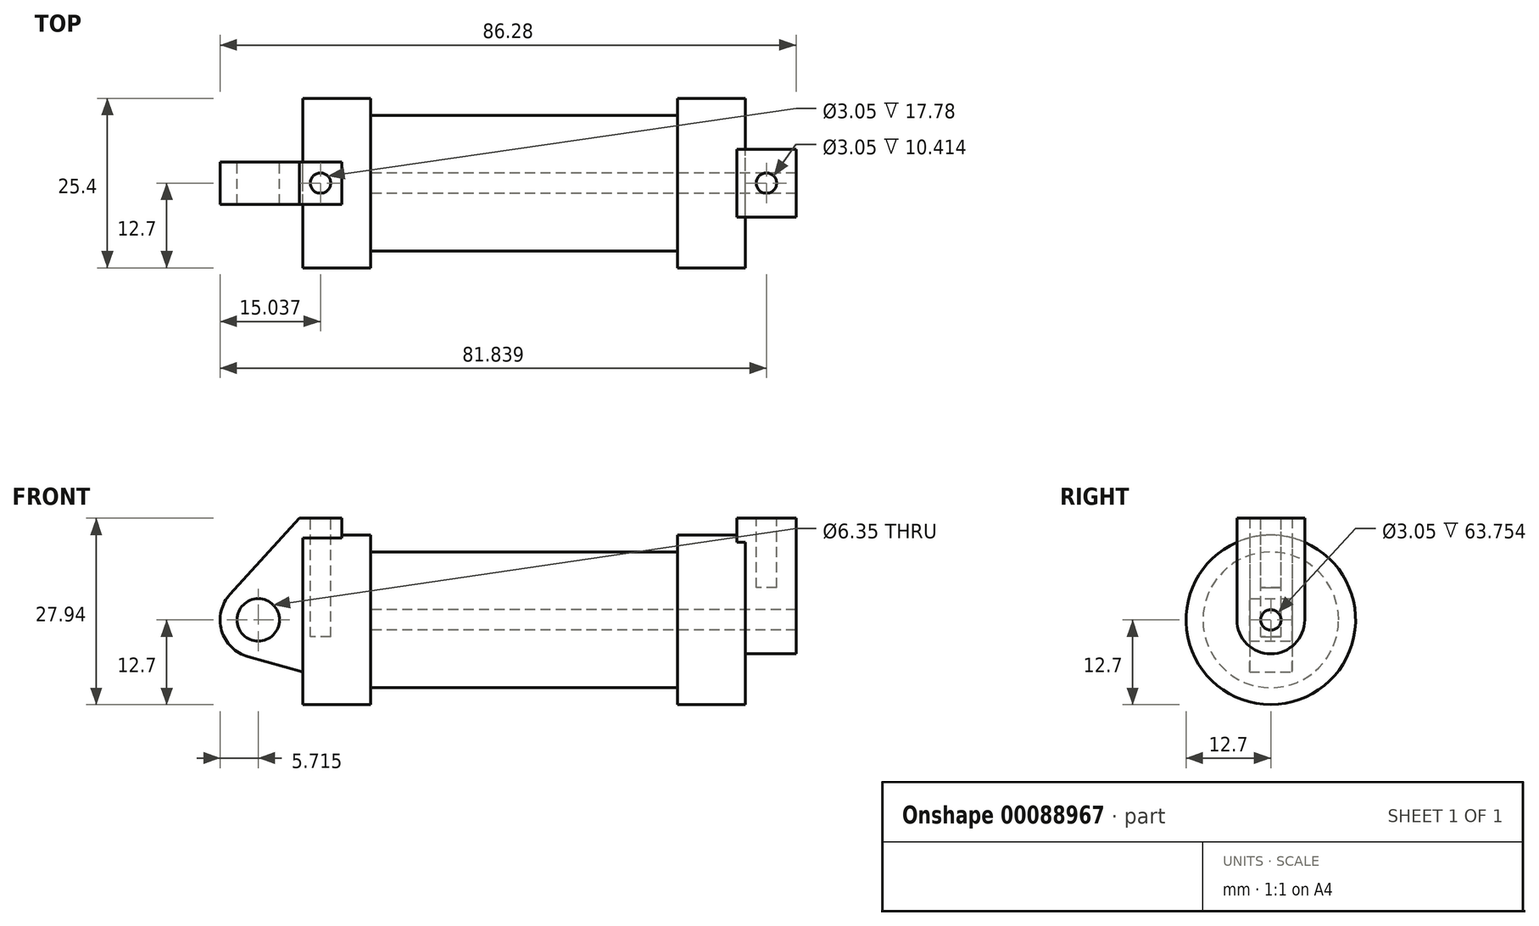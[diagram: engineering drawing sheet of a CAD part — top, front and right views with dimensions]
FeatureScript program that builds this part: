
annotation { "Feature Type Name" : "Feature", "Feature Type Description" : "" }
export const myFeature = defineFeature(function(context is Context, id is Id, definition is map)
    precondition{}
    {
        {
            var Q0;
            Q0=qCreatedBy(makeId("Front.planeOp"),FACE);
            var sketch = newSketch(context, id + "F0", { "sketchPlane" : qUnion([Q0])});
            skLineSegment(sketch, "E0", {"start": v(0, 0) * mm, "end": v(0, 12.7) * mm});
            skLineSegment(sketch, "E1", {"start": v(0, 12.7) * mm, "end": v(10.16, 12.7) * mm});
            skLineSegment(sketch, "E2", {"start": v(10.16, 12.7) * mm, "end": v(10.16, 10.16) * mm});
            skLineSegment(sketch, "E3", {"start": v(10.16, 10.16) * mm, "end": v(56.13, 10.16) * mm});
            skLineSegment(sketch, "E4", {"start": v(56.13, 10.16) * mm, "end": v(56.13, 12.7) * mm});
            skLineSegment(sketch, "E5", {"start": v(56.13, 12.7) * mm, "end": v(66.3, 12.7) * mm});
            skLineSegment(sketch, "E6", {"start": v(66.3, 12.7) * mm, "end": v(66.3, 0) * mm});
            skLineSegment(sketch, "E7", {"start": v(66.3, 0) * mm, "end": v(0, 0) * mm});
            skLineSegment(sketch, "E8", {"start": v(5.84, 15.24) * mm, "end": v(-0.5, 15.24) * mm});
            skLineSegment(sketch, "E9", {"start": v(-0.5, 15.24) * mm, "end": v(-10.88, 3.85) * mm});
            skLineSegment(sketch, "E10", {"start": v(0, 0) * mm, "end": v(-6.65, 0) * mm});
            skCircle(sketch, "E11", {"center": v(-6.65, 0) * mm, "radius": 5.72 * mm});
            skCircle(sketch, "E12", {"center": v(-6.65, 0) * mm, "radius": 3.18 * mm});
            skLineSegment(sketch, "E13", {"start": v(5.84, 15.24) * mm, "end": v(5.84, -9.4) * mm});
            skLineSegment(sketch, "E14", {"start": v(5.84, -9.4) * mm, "end": v(-8.18, -5.5) * mm});
            skSolve(sketch);
        }
        {
            var Q0;
            {var subQ0=sQuery(id+"F0.wireOp",EDGE,"E0");Q0=makeQuery(id+"F0.imprint","IMPRINT",FACE,{"disambiguationData":[TD([[makeQuery(id+"F0.imprint","IMPRINT",EDGE,{"derivedFrom":subQ0}),-1.0]])]});}
            var Q1;
            {var subQ0=sQuery(id+"F0.wireOp",EDGE,"E2");Q1=makeQuery(id+"F0.imprint","IMPRINT",FACE,{"disambiguationData":[TD([[makeQuery(id+"F0.imprint","IMPRINT",EDGE,{"derivedFrom":subQ0}),-1.0]])]});}
            var Q2;
            Q2=sQuery(id+"F0.wireOp",EDGE,"E7");
            revolve(context, id + "F1", {"entities" : qUnion([Q0, Q1]), "axis" : qUnion([Q2]), "revolveType" : RevolveType.FULL});
        }
        {
            var Q0;
            {var subQ3=sQuery(id+"F0.wireOp",EDGE,"E0");Q0=makeQuery(id+"F0.imprint","IMPRINT",FACE,{"disambiguationData":[TD([[makeQuery(id+"F0.imprint","IMPRINT",EDGE,{"derivedFrom":subQ3}),1.0]])]});}
            var Q1;
            {var subQ4=sQuery(id+"F0.wireOp",EDGE,"E12");Q1=makeQuery(id+"F0.imprint","IMPRINT",FACE,{"disambiguationData":[TD([[makeQuery(id+"F0.imprint","IMPRINT",EDGE,{"derivedFrom":subQ4}),-1.0]])]});}
            var Q2;
            {var subQ0=sQuery(id+"F0.wireOp",EDGE,"E14");Q2=makeQuery(id+"F0.imprint","IMPRINT",FACE,{"disambiguationData":[TD([[makeQuery(id+"F0.imprint","IMPRINT",EDGE,{"derivedFrom":subQ0}),-1.0]])]});}
            var Q3;
            {var subQ0=sQuery(id+"F0.wireOp",EDGE,"E0");Q3=makeQuery(id+"F0.imprint","IMPRINT",FACE,{"disambiguationData":[TD([[makeQuery(id+"F0.imprint","IMPRINT",EDGE,{"derivedFrom":subQ0}),-1.0]])]});}
            extrude(context, id + "F2", {"entities" : qUnion([Q0, Q1, Q2, Q3]), "operationType" : NewBodyOperationType.ADD, "endBound" : BoundingType.SYMMETRIC, "depth" : 6.35 * mm});
        }
        {
            var Q0;
            Q0=makeQuery(id+"F1.opRevolve","SWEPT_FACE",FACE,{"disambiguationData":[OSD([sQuery(id+"F0.wireOp",EDGE,"E6")])]});
            var sketch = newSketch(context, id + "F3", { "sketchPlane" : qUnion([Q0])});
            skCircle(sketch, "E15", {"center": v(0, 0) * mm, "radius": 5.08 * mm});
            skCircle(sketch, "E16", {"center": v(0, 0) * mm, "radius": 1.52 * mm});
            skLineSegment(sketch, "E17", {"start": v(-5.08, 0) * mm, "end": v(-5.08, 15.24) * mm});
            skLineSegment(sketch, "E18", {"start": v(5.08, 0) * mm, "end": v(5.08, 15.24) * mm});
            skLineSegment(sketch, "E19", {"start": v(5.08, 15.24) * mm, "end": v(-5.08, 15.24) * mm});
            skSolve(sketch);
        }
        {
            var Q0;
            Q0=makeQuery(id+"F3.imprint","IMPRINT",FACE,{"disambiguationData":[TD([[makeQuery(id+"F3.imprint","IMPRINT",EDGE,{"derivedFrom":sQuery(id+"F3.wireOp",EDGE,"E16")}),-1.0]])]});
            var Q1;
            {var subQ0=sQuery(id+"F3.wireOp",EDGE,"E17");var subQ1=sQuery(id+"F3.wireOp",EDGE,"E15");var subQ2=makeQuery(id+"F3.imprint","INTERSECT",VERTEX,{"derivedFrom":[subQ1,subQ0]});Q1=makeQuery(id+"F3.imprint","IMPRINT",FACE,{"disambiguationData":[TD([[makeQuery(id+"F3.imprint","IMPRINT",EDGE,{"disambiguationData":[TD([[subQ2,1.0]])],"derivedFrom":subQ1}),-1.0]])]});}
            var Q2;
            {var subQ0=sQuery(id+"F3.wireOp",EDGE,"E19");Q2=makeQuery(id+"F3.imprint","IMPRINT",FACE,{"disambiguationData":[TD([[makeQuery(id+"F3.imprint","IMPRINT",EDGE,{"derivedFrom":subQ0}),1.0]])]});}
            extrude(context, id + "F4", {"entities" : qUnion([Q0, Q1, Q2]), "operationType" : NewBodyOperationType.ADD, "depth" : 7.62 * mm});
        }
        {
            var Q0;
            Q0=makeQuery(id+"F4.opExtrude","CAP_FACE",FACE,{"disambiguationData":[OSD([sQuery(id+"F3.wireOp",EDGE,"E15"),sQuery(id+"F3.wireOp",EDGE,"E16"),sQuery(id+"F3.wireOp",EDGE,"E17"),sQuery(id+"F3.wireOp",EDGE,"E18"),sQuery(id+"F3.wireOp",EDGE,"E19")])],"isStart":true});
            extrude(context, id + "F5", {"entities" : qUnion([Q0]), "operationType" : NewBodyOperationType.ADD, "depth" : 1.27 * mm});
        }
        {
            var Q0;
            Q0=makeQuery(id+"F4.boolean.opBoolean","SPLIT",FACE,{"disambiguationData":[TD([makeQuery(id+"F4.opExtrude","SWEPT_FACE",FACE,{"disambiguationData":[OSD([sQuery(id+"F3.wireOp",EDGE,"E16")])]})])],"derivedFrom":makeQuery(id+"F1.opRevolve","SWEPT_FACE",FACE,{"disambiguationData":[OSD([sQuery(id+"F0.wireOp",EDGE,"E6")])]})});
            var Q1;
            Q1=makeQuery(id+"F1.opRevolve","SWEPT_FACE",FACE,{"disambiguationData":[OSD([sQuery(id+"F0.wireOp",EDGE,"E2")])]});
            extrude(context, id + "F6", {"entities" : qUnion([Q0]), "operationType" : NewBodyOperationType.REMOVE, "endBound" : BoundingType.UP_TO_SURFACE, "oppositeDirection" : true, "endBoundEntityFace" : qUnion([Q1]), "depth" : 25.4 * mm});
        }
        {
            var Q0;
            Q0=makeQuery(id+"F2.opExtrude","SWEPT_FACE",FACE,{"disambiguationData":[OSD([sQuery(id+"F0.wireOp",EDGE,"E8")])]});
            var sketch = newSketch(context, id + "F7", { "sketchPlane" : qUnion([Q0])});
            skLineSegment(sketch, "E20.0.0", {"start": v(5.84, 3.18) * mm, "end": v(-0.5, 3.18) * mm});
            skLineSegment(sketch, "E20.0.1", {"start": v(-0.5, 3.17) * mm, "end": v(-0.5, -3.18) * mm});
            skLineSegment(sketch, "E20.0.2", {"start": v(-0.5, -3.18) * mm, "end": v(5.84, -3.18) * mm});
            skLineSegment(sketch, "E20.0.3", {"start": v(5.84, -3.18) * mm, "end": v(5.84, 3.17) * mm});
            skCircle(sketch, "E21", {"center": v(2.67, 0) * mm, "radius": 1.52 * mm});
            skLineSegment(sketch, "E22.0.0", {"start": v(73.91, 5.08) * mm, "end": v(65.02, 5.08) * mm});
            skLineSegment(sketch, "E22.0.1", {"start": v(65.02, 5.08) * mm, "end": v(65.02, -5.08) * mm});
            skLineSegment(sketch, "E22.0.2", {"start": v(65.02, -5.08) * mm, "end": v(73.91, -5.08) * mm});
            skLineSegment(sketch, "E22.0.3", {"start": v(73.91, -5.08) * mm, "end": v(73.91, 5.08) * mm});
            skCircle(sketch, "E23", {"center": v(69.47, 0) * mm, "radius": 1.52 * mm});
            skSolve(sketch);
        }
        {
            var Q0;
            Q0=makeQuery(id+"F7.imprint","IMPRINT",FACE,{"disambiguationData":[TD([[makeQuery(id+"F7.imprint","IMPRINT",EDGE,{"derivedFrom":sQuery(id+"F7.wireOp",EDGE,"E21")}),1.0]])]});
            extrude(context, id + "F8", {"entities" : qUnion([Q0]), "operationType" : NewBodyOperationType.REMOVE, "oppositeDirection" : true, "depth" : 17.78 * mm});
        }
        {
            var Q0;
            Q0=makeQuery(id+"F7.imprint","IMPRINT",FACE,{"disambiguationData":[TD([[makeQuery(id+"F7.imprint","IMPRINT",EDGE,{"derivedFrom":sQuery(id+"F7.wireOp",EDGE,"E23")}),1.0]])]});
            extrude(context, id + "F9", {"entities" : qUnion([Q0]), "operationType" : NewBodyOperationType.REMOVE, "oppositeDirection" : true, "depth" : 10.4 * mm});
        }
    });
